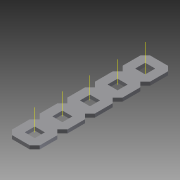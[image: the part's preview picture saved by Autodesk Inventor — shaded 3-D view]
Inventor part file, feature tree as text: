
AUTODESK INVENTOR PART (.ipt)
format: ipt  version: 2015 (Build 190159000, 159)  size: 1,067,008 bytes
history: native  units: in
note: dims shown in document units (in); Inventor stores cm internally (conversion verified against a paired STEP export)
features: other x14, extrude x2, pattern_linear x1, imported_body x1
ambient origin geometry x8: Origin, YZ Plane, XZ Plane, XY Plane, X Axis, Y Axis, Z Axis, Center Point
bodies: Body1 (feature_tree)
feature tree (18):
  other  "Diamond-Pattern"
  other  "Plate"
  extrude  "length cut"  TaperAngle=0.0deg  [1 undecoded]
  extrude  "width cut"  TaperAngle=0.0deg  [1 undecoded]
  other  "constraint axis"
  pattern_linear  "constraint axes"  Spacing1=0.5in  [1 undecoded]
  other  "front plane"
  other  "right plane"
  imported_body  "Base1"
  other  "length profile"
  other  "width profile"
  other  "Work Point1"
  other  "back plane"
  other  "left plane"
  other  "Work Axis170"
  other  "Work Axis171"
  other  "Work Axis172"
  other  "Work Axis173"
note: 3 required parameter values undecoded (feature->parameter linkage not recoverable at this tier; creation-order binding heuristic only, values carry confidence <= 0.55)
